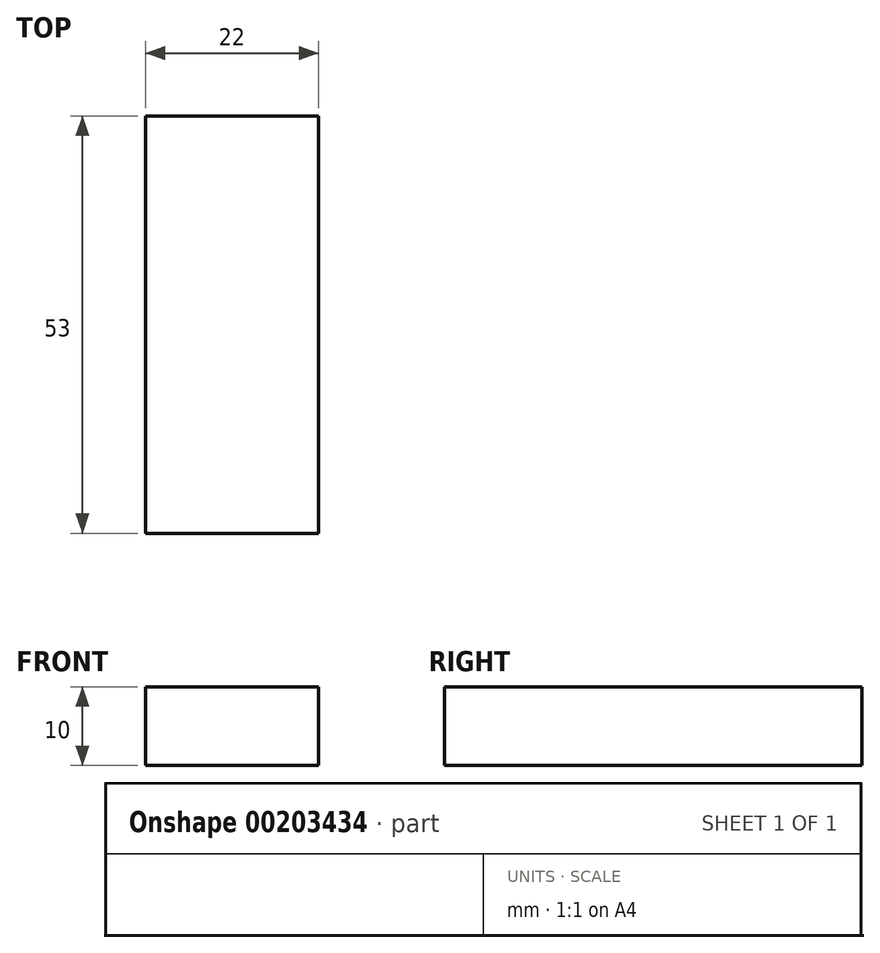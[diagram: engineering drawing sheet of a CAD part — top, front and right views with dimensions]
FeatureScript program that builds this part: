
annotation { "Feature Type Name" : "Feature", "Feature Type Description" : "" }
export const myFeature = defineFeature(function(context is Context, id is Id, definition is map)
    precondition{}
    {
        {
            var Q0;
            Q0=qCreatedBy(makeId("Top.planeOp"),FACE);
            var sketch = newSketch(context, id + "F0", { "sketchPlane" : qUnion([Q0])});
            skLineSegment(sketch, "E0.bottom", {"start": v(-29.7, 29.7) * mm, "end": v(29.7, 29.7) * mm});
            skLineSegment(sketch, "E0.top", {"start": v(-29.7, -29.7) * mm, "end": v(29.7, -29.7) * mm});
            skLineSegment(sketch, "E0.left", {"start": v(-29.7, 29.7) * mm, "end": v(-29.7, -29.7) * mm});
            skLineSegment(sketch, "E0.right", {"start": v(29.7, 29.7) * mm, "end": v(29.7, -29.7) * mm});
            skPoint(sketch, "E1", {"position": v(0, 29.7) * mm});
            skPoint(sketch, "E2", {"position": v(-29.7, 0) * mm});
            skLineSegment(sketch, "E3.bottom", {"start": v(-23.3, 23.3) * mm, "end": v(23.3, 23.3) * mm});
            skLineSegment(sketch, "E3.top", {"start": v(-23.3, -23.3) * mm, "end": v(23.3, -23.3) * mm});
            skLineSegment(sketch, "E3.left", {"start": v(-23.3, 23.3) * mm, "end": v(-23.3, -23.3) * mm});
            skLineSegment(sketch, "E3.right", {"start": v(23.3, 23.3) * mm, "end": v(23.3, -23.3) * mm});
            skPoint(sketch, "E4", {"position": v(0, 23.3) * mm});
            skPoint(sketch, "E5", {"position": v(-23.3, 0) * mm});
            skCircle(sketch, "E6.cCircle", {"center": v(-29.7, 29.7) * mm, "radius": 18.7 * mm, "construction": true});
            skLineSegment(sketch, "E6.0", {"start": v(-33.42, 48.4) * mm, "end": v(-25.98, 48.4) * mm});
            skLineSegment(sketch, "E6.1", {"start": v(-25.98, 48.4) * mm, "end": v(-19.1, 45.55) * mm});
            skLineSegment(sketch, "E6.2", {"start": v(-19.1, 45.55) * mm, "end": v(-13.85, 40.3) * mm});
            skLineSegment(sketch, "E6.3", {"start": v(-13.85, 40.3) * mm, "end": v(-11, 33.42) * mm});
            skLineSegment(sketch, "E6.4", {"start": v(-11, 33.42) * mm, "end": v(-11, 25.98) * mm});
            skLineSegment(sketch, "E6.5", {"start": v(-11, 25.98) * mm, "end": v(-13.85, 19.1) * mm});
            skLineSegment(sketch, "E6.6", {"start": v(-13.85, 19.1) * mm, "end": v(-19.1, 13.85) * mm});
            skLineSegment(sketch, "E6.7", {"start": v(-19.1, 13.85) * mm, "end": v(-25.98, 11) * mm});
            skLineSegment(sketch, "E6.8", {"start": v(-25.98, 11) * mm, "end": v(-33.42, 11) * mm});
            skLineSegment(sketch, "E6.9", {"start": v(-33.42, 11) * mm, "end": v(-40.3, 13.85) * mm});
            skLineSegment(sketch, "E6.10", {"start": v(-40.3, 13.85) * mm, "end": v(-45.55, 19.1) * mm});
            skLineSegment(sketch, "E6.11", {"start": v(-45.55, 19.1) * mm, "end": v(-48.4, 25.98) * mm});
            skLineSegment(sketch, "E6.12", {"start": v(-48.4, 25.98) * mm, "end": v(-48.4, 33.42) * mm});
            skLineSegment(sketch, "E6.13", {"start": v(-48.4, 33.42) * mm, "end": v(-45.55, 40.3) * mm});
            skLineSegment(sketch, "E6.14", {"start": v(-45.55, 40.3) * mm, "end": v(-40.3, 45.55) * mm});
            skLineSegment(sketch, "E6.15", {"start": v(-40.3, 45.55) * mm, "end": v(-33.42, 48.4) * mm});
            skPoint(sketch, "E6.0.midPoint", {"position": v(-29.7, 48.4) * mm});
            skLineSegment(sketch, "E7.1.0", {"start": v(-11, -25.98) * mm, "end": v(-11, -33.42) * mm});
            skLineSegment(sketch, "E7.1.1", {"start": v(-13.85, -19.1) * mm, "end": v(-11, -25.98) * mm});
            skLineSegment(sketch, "E7.1.2", {"start": v(-19.1, -13.85) * mm, "end": v(-13.85, -19.1) * mm});
            skLineSegment(sketch, "E7.1.3", {"start": v(-25.98, -11) * mm, "end": v(-19.1, -13.85) * mm});
            skLineSegment(sketch, "E7.1.4", {"start": v(-33.42, -11) * mm, "end": v(-25.98, -11) * mm});
            skLineSegment(sketch, "E7.2.0", {"start": v(25.98, -11) * mm, "end": v(33.42, -11) * mm});
            skLineSegment(sketch, "E7.2.1", {"start": v(19.1, -13.85) * mm, "end": v(25.98, -11) * mm});
            skLineSegment(sketch, "E7.2.2", {"start": v(13.85, -19.1) * mm, "end": v(19.1, -13.85) * mm});
            skLineSegment(sketch, "E7.2.3", {"start": v(11, -25.98) * mm, "end": v(13.85, -19.1) * mm});
            skLineSegment(sketch, "E7.2.4", {"start": v(11, -33.42) * mm, "end": v(11, -25.98) * mm});
            skLineSegment(sketch, "E7.3.0", {"start": v(11, 25.98) * mm, "end": v(11, 33.42) * mm});
            skLineSegment(sketch, "E7.3.1", {"start": v(13.85, 19.1) * mm, "end": v(11, 25.98) * mm});
            skLineSegment(sketch, "E7.3.2", {"start": v(19.1, 13.85) * mm, "end": v(13.85, 19.1) * mm});
            skLineSegment(sketch, "E7.3.3", {"start": v(25.98, 11) * mm, "end": v(19.1, 13.85) * mm});
            skLineSegment(sketch, "E7.3.4", {"start": v(33.42, 11) * mm, "end": v(25.98, 11) * mm});
            skPoint(sketch, "E7.center", {"position": v(0, 0) * mm});
            skSolve(sketch);
        }
        {
            var Q0;
            Q0=qCreatedBy(makeId("Right.planeOp"),FACE);
            var Q1;
            Q1=sQuery(id+"F0.wireOp",VERTEX,"E3.top.start");
            cPlane(context, id + "F1", {"entities" : qUnion([Q0, Q1]), "cplaneType" : CPlaneType.PLANE_POINT, "offset" : 25 * mm, "width" : 150 * mm, "height" : 150 * mm});
        }
        {
            var Q0;
            Q0=qCreatedBy(makeId("Top.planeOp"),FACE);
            var sketch = newSketch(context, id + "F2", { "sketchPlane" : qUnion([Q0])});
            skLineSegment(sketch, "E8.0", {"start": v(-29.7, 29.7) * mm, "end": v(-29.7, -29.7) * mm});
            skLineSegment(sketch, "E9.0", {"start": v(-23.3, 23.3) * mm, "end": v(-23.3, -23.3) * mm});
            skLineSegment(sketch, "E10.0", {"start": v(23.3, 23.3) * mm, "end": v(23.3, -23.3) * mm});
            skLineSegment(sketch, "E11.0", {"start": v(29.7, 29.7) * mm, "end": v(29.7, -29.7) * mm});
            skPoint(sketch, "E12.0", {"position": v(-29.7, 11) * mm});
            skPoint(sketch, "E13.0", {"position": v(-29.7, -11) * mm});
            skPoint(sketch, "E14.0", {"position": v(29.7, -11) * mm});
            skPoint(sketch, "E15.0", {"position": v(29.7, 11) * mm});
            skLineSegment(sketch, "E16.bottom", {"start": v(-29.7, 11) * mm, "end": v(29.7, 11) * mm});
            skLineSegment(sketch, "E16.top", {"start": v(-29.7, -11) * mm, "end": v(29.7, -11) * mm});
            skLineSegment(sketch, "E16.left", {"start": v(-29.7, 11) * mm, "end": v(-29.7, -11) * mm});
            skLineSegment(sketch, "E16.right", {"start": v(29.7, 11) * mm, "end": v(29.7, -11) * mm});
            skLineSegment(sketch, "E17.0.0", {"start": v(12.11, 23.3) * mm, "end": v(-12.11, 23.3) * mm});
            skLineSegment(sketch, "E17.0.1", {"start": v(-12.11, 23.3) * mm, "end": v(-13.85, 19.1) * mm});
            skLineSegment(sketch, "E17.0.2", {"start": v(-13.85, 19.1) * mm, "end": v(-19.1, 13.85) * mm});
            skLineSegment(sketch, "E17.0.3", {"start": v(-19.1, 13.85) * mm, "end": v(-23.3, 12.11) * mm});
            skLineSegment(sketch, "E17.0.4", {"start": v(-23.3, 12.11) * mm, "end": v(-23.3, -12.11) * mm});
            skLineSegment(sketch, "E17.0.5", {"start": v(-23.3, -12.11) * mm, "end": v(-19.1, -13.85) * mm});
            skLineSegment(sketch, "E17.0.6", {"start": v(-19.1, -13.85) * mm, "end": v(-13.85, -19.1) * mm});
            skLineSegment(sketch, "E17.0.7", {"start": v(-13.85, -19.1) * mm, "end": v(-12.11, -23.3) * mm});
            skLineSegment(sketch, "E17.0.8", {"start": v(-12.11, -23.3) * mm, "end": v(12.11, -23.3) * mm});
            skLineSegment(sketch, "E17.0.9", {"start": v(12.11, -23.3) * mm, "end": v(13.85, -19.1) * mm});
            skLineSegment(sketch, "E17.0.10", {"start": v(13.85, -19.1) * mm, "end": v(19.1, -13.85) * mm});
            skLineSegment(sketch, "E17.0.11", {"start": v(19.1, -13.85) * mm, "end": v(23.3, -12.11) * mm});
            skLineSegment(sketch, "E17.0.12", {"start": v(23.3, -12.11) * mm, "end": v(23.3, 12.11) * mm});
            skLineSegment(sketch, "E17.0.13", {"start": v(23.3, 12.11) * mm, "end": v(19.1, 13.85) * mm});
            skLineSegment(sketch, "E17.0.14", {"start": v(19.1, 13.85) * mm, "end": v(13.85, 19.1) * mm});
            skLineSegment(sketch, "E17.0.15", {"start": v(13.85, 19.1) * mm, "end": v(12.11, 23.3) * mm});
            skPoint(sketch, "E18", {"position": v(-23.3, 11) * mm});
            skPoint(sketch, "E19", {"position": v(23.3, 11) * mm});
            skPoint(sketch, "E20", {"position": v(23.3, -11) * mm});
            skPoint(sketch, "E21", {"position": v(-23.3, -11) * mm});
            skPoint(sketch, "E22", {"position": v(-13.9, 11) * mm});
            skLineSegment(sketch, "E23.0", {"start": v(-29.7, -29.7) * mm, "end": v(29.7, -29.7) * mm});
            skLineSegment(sketch, "E24.0", {"start": v(-29.7, 29.7) * mm, "end": v(29.7, 29.7) * mm});
            skPoint(sketch, "E25", {"position": v(-12.11, 29.7) * mm});
            skLineSegment(sketch, "E26.0", {"start": v(-11, -25.98) * mm, "end": v(-11, -33.42) * mm});
            skPoint(sketch, "E27", {"position": v(-11, -29.7) * mm});
            skPoint(sketch, "E28.MirrorP", {"position": v(11, -29.7) * mm});
            skPoint(sketch, "E29.MirrorP", {"position": v(11, 29.7) * mm});
            skPoint(sketch, "E30.MirrorP", {"position": v(-11, 29.7) * mm});
            skLineSegment(sketch, "E31", {"start": v(-11, -29.7) * mm, "end": v(-11, 29.7) * mm});
            skLineSegment(sketch, "E32", {"start": v(11, 29.7) * mm, "end": v(11, -29.7) * mm});
            skSolve(sketch);
        }
        {
            var Q0;
            Q0=qCreatedBy(id+"F1.planeOp",FACE);
            var sketch = newSketch(context, id + "F3", { "sketchPlane" : qUnion([Q0])});
            skPoint(sketch, "E33.0", {"position": v(-29.7, 0) * mm});
            skPoint(sketch, "E34.0", {"position": v(29.7, 0) * mm});
            skLineSegment(sketch, "E35.0", {"start": v(29.7, 0) * mm, "end": v(-29.7, 0) * mm});
            skLineSegment(sketch, "E36", {"start": v(-29.7, 0) * mm, "end": v(0, 29.7) * mm});
            skLineSegment(sketch, "E37", {"start": v(0, 29.7) * mm, "end": v(29.7, 0) * mm});
            skCircle(sketch, "E38", {"center": v(0, 29.7) * mm, "radius": 3.2 * mm});
            skCircle(sketch, "E39", {"center": v(0, 29.7) * mm, "radius": 12.6 * mm});
            skPoint(sketch, "E40", {"position": v(0, 7.35) * mm});
            skSolve(sketch);
        }
        {
            var Q0;
            {var subQ0=sQuery(id+"F2.wireOp",EDGE,"E31");var subQ1=sQuery(id+"F2.wireOp",EDGE,"E16.bottom");var subQ2=makeQuery(id+"F2.imprint","INTERSECT",VERTEX,{"derivedFrom":[subQ1,subQ0]});Q0=makeQuery(id+"F2.imprint","IMPRINT",FACE,{"disambiguationData":[TD([[makeQuery(id+"F2.imprint","IMPRINT",EDGE,{"disambiguationData":[TD([[subQ2,-1.0]])],"derivedFrom":subQ1}),1.0]])]});}
            var Q1;
            {var subQ0=sQuery(id+"F2.wireOp",EDGE,"E31");var subQ1=sQuery(id+"F2.wireOp",EDGE,"E16.bottom");var subQ2=makeQuery(id+"F2.imprint","INTERSECT",VERTEX,{"derivedFrom":[subQ1,subQ0]});Q1=makeQuery(id+"F2.imprint","IMPRINT",FACE,{"disambiguationData":[TD([[makeQuery(id+"F2.imprint","IMPRINT",EDGE,{"disambiguationData":[TD([[subQ2,-1.0]])],"derivedFrom":subQ1}),-1.0]])]});}
            var Q2;
            {var subQ0=sQuery(id+"F2.wireOp",EDGE,"E31");var subQ1=sQuery(id+"F2.wireOp",EDGE,"E16.top");var subQ2=makeQuery(id+"F2.imprint","INTERSECT",VERTEX,{"derivedFrom":[subQ1,subQ0]});Q2=makeQuery(id+"F2.imprint","IMPRINT",FACE,{"disambiguationData":[TD([[makeQuery(id+"F2.imprint","IMPRINT",EDGE,{"disambiguationData":[TD([[subQ2,-1.0]])],"derivedFrom":subQ1}),-1.0]])]});}
            var Q3;
            {var subQ0=sQuery(id+"F2.wireOp",EDGE,"E31");var subQ1=makeQuery(id+"F2.imprint","IMPRINT",VERTEX,{"derivedFrom":subQ0});Q3=makeQuery(id+"F2.imprint","IMPRINT",FACE,{"disambiguationData":[TD([[makeQuery(id+"F2.imprint","IMPRINT",EDGE,{"disambiguationData":[TD([[subQ1,1.0]])],"derivedFrom":subQ0}),-1.0]])]});}
            var Q4;
            {var subQ0=sQuery(id+"F2.wireOp",EDGE,"E32");var subQ1=sQuery(id+"F2.wireOp",EDGE,"E17.0.0");var subQ2=makeQuery(id+"F2.imprint","INTERSECT",VERTEX,{"derivedFrom":[subQ1,subQ0]});Q4=makeQuery(id+"F2.imprint","IMPRINT",FACE,{"disambiguationData":[TD([[makeQuery(id+"F2.imprint","IMPRINT",EDGE,{"disambiguationData":[TD([[subQ2,-1.0]])],"derivedFrom":subQ1}),-1.0]])]});}
            extrude(context, id + "F4", {"entities" : qUnion([Q0, Q1, Q2, Q3, Q4]), "endBound" : BoundingType.SYMMETRIC, "depth" : 10 * mm});
        }
    });
